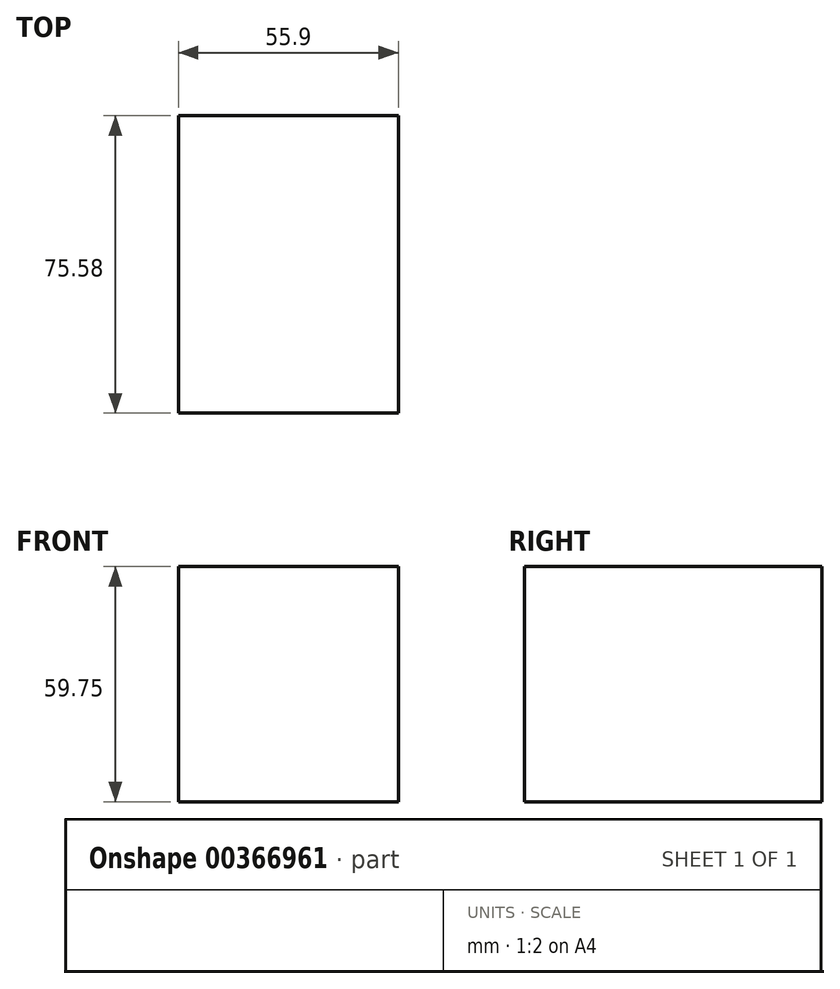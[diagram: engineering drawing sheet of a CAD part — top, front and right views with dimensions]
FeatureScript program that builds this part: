
annotation { "Feature Type Name" : "Feature", "Feature Type Description" : "" }
export const myFeature = defineFeature(function(context is Context, id is Id, definition is map)
    precondition{}
    {
        {
            var Q0;
            Q0=qCreatedBy(makeId("Front.planeOp"),FACE);
            var sketch = newSketch(context, id + "F0", { "sketchPlane" : qUnion([Q0])});
            skLineSegment(sketch, "E0.bottom", {"start": v(0, 0) * mm, "end": v(30.5, 0) * mm});
            skLineSegment(sketch, "E0.top", {"start": v(0, -59.75) * mm, "end": v(30.5, -59.75) * mm});
            skLineSegment(sketch, "E0.left", {"start": v(0, 0) * mm, "end": v(0, -59.75) * mm});
            skLineSegment(sketch, "E0.right", {"start": v(30.5, 0) * mm, "end": v(30.5, -59.75) * mm});
            skSolve(sketch);
        }
        {
            var Q0;
            Q0=makeQuery(id+"F0.imprint","IMPRINT",FACE,{"disambiguationData":[TD([[makeQuery(id+"F0.imprint","IMPRINT",EDGE,{"derivedFrom":sQuery(id+"F0.wireOp",EDGE,"E0.bottom")}),-1.0]])]});
            extrude(context, id + "F1", {"entities" : qUnion([Q0]), "depth" : 75.58 * mm});
        }
        {
            var Q0;
            Q0=makeQuery(id+"F1.opExtrude","SWEPT_FACE",FACE,{"disambiguationData":[OSD([sQuery(id+"F0.wireOp",EDGE,"E0.right")])]});
            extrude(context, id + "F2", {"entities" : qUnion([Q0]), "operationType" : NewBodyOperationType.ADD, "depth" : 25.4 * mm});
        }
    });
